# Revit family: BDG_BossDesign_Stng_Kruze_Stool
name_source: partatom
category: Furniture
revit_build: Autodesk Revit 2015 (Build: 20140903_1530(x64)
units: mm (PartAtom-declared; Revit-internal decimal feet)

## types (6) — shared parameters
Assembly Code = E2020200
AssetType = Movable
BIMObjectName = BDG_BossDesign_Seating_Kruze_Stool
Category = Pr_40_50_12_85 : Stools
CodePerformance = BS EN13761: 2002
DurationUnit = year
ExpectedLife = 5
Features = 4 Leg
IfcExportAs = IfcFurnishingElementType
IfcExportType = STOOL
Keynote = Pr_40_50_12_85
ManufacturerName = Boss Design
ManufacturerURL = www.bossdesign.com
NBSDescription = Seating
NBSReference = 45-35-72/352
Name = Seating_Kruze_Stool_BossDesign
NominalLength = 540 mm  [stored 1.77165 ft]
NominalWidth = 510 mm  [stored 1.67323 ft]
ProductInformation = www.bossdesign.com/product-list/kruze-bar-stool/
Revision = 1
Shape = Rectangular
SustainabilityPerformance = 85.85% Recyclable
URL = www.bossdesign.com
Uniclass2015Description = Stools
Uniclass2015Reference = Pr_40_50_12_85
Uniclass2015Version = Products v1.9
Version = 1
WarrantyDescription = Structural Warranty Excludes Foams and Fabrics
WarrantyDurationLabor = 5
WarrantyDurationParts = 5
WarrantyDurationUnit = year

## per-type parameters (varying)
| type | Finish | HasBack | HasNoBack | IsUpholsteredShell | IsUpholsteredShellBack | IsWoodShell | IsWoodShellBack | Material | Model | ModelNumber | NominalHeight | ShellMaterial | Size |
| Fully Upholstered Stool with Back 4 Leg | Upholstered | Yes | No | Yes | Yes | No | No | Fabric | KRU/7 | KRU/7 | 1060 mm  [stored 3.47769 ft] | BDG_Generic_Wood_Oak | 540 x 510 x 1060mm |
| Oak Outershell Stool with Back 4 Leg | Oak Outershell | Yes | No | No | No | Yes | Yes | Wood | KRU/8/O | KRU/8/O | 1060 mm  [stored 3.47769 ft] | BDG_Generic_Wood_Oak | 540 x 510 x 1060mm |
| Walnut Outershell Stool with Back 4 Leg | Walnut Outershell | Yes | No | No | No | Yes | Yes | Wood | KRU/8/W | KRU/8/W | 1060 mm  [stored 3.47769 ft] | BDG_Generic_Wood_Walnut_BlackAmerican | 540 x 510 x 1060mm |
| Fully Upholstered Stool No Back 4 Leg | Upholstered | No | Yes | Yes | No | No | No | Fabric | KRU/9 | KRU/9 | 820 mm  [stored 2.69029 ft] | BDG_Generic_Wood_Oak | 540 x 510 x 820mm |
| Oak Outershell Stool No Back 4 Leg | Oak Outershell | No | Yes | No | No | Yes | No | Wood | KRU/10/O | KRU/10/O | 820 mm  [stored 2.69029 ft] | BDG_Generic_Wood_Oak | 540 x 510 x 820mm |
| Walnut Outershell Stool no Back 4 Leg | Walnut Outershell | No | Yes | No | No | Yes | No | Wood | KRU/10/W | KRU/10/W | 820 mm  [stored 2.69029 ft] | BDG_Generic_Wood_Walnut_BlackAmerican | 540 x 510 x 820mm |

note: column(s) folded — value = type name in every type: Description, ModelReference

note: [stored X ft] marks values corroborated as IEEE doubles in the binary element streams (Revit-internal decimal feet)

## geometry (parser evidence)
native form markers: Blend x170, Sweep x3
no freeform markers — native parametric forms only
